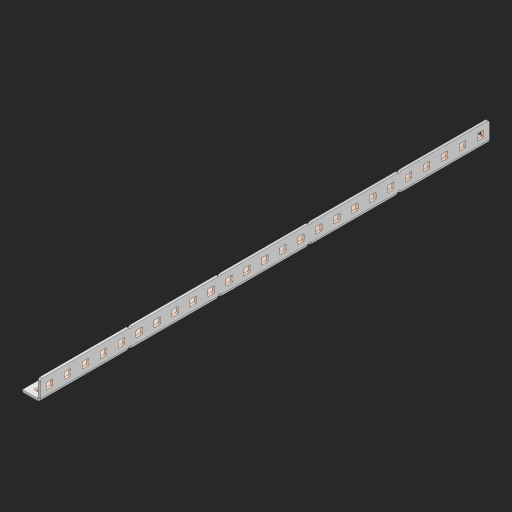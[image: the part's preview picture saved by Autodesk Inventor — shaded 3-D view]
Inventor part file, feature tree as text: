
AUTODESK INVENTOR PART (.ipt)
format: ipt  version: 2023 (Build 270158000, 158)  size: 854,528 bytes
history: native  units: in
note: dims shown in document units (in); Inventor stores cm internally (conversion verified against a paired STEP export)
features: other x55, extrude x49, sheet_metal_op x10, sketch x8, mirror x1, pattern_linear x1, chamfer x1
ambient origin geometry x8: Origin, YZ Plane, XZ Plane, XY Plane, X Axis, Y Axis, Z Axis, Center Point
bodies: Solid1 (feature_tree), Body (feature_tree)
feature tree (125):
  other  "Flange Pattern Plane"
  sheet_metal_op  "Flange Pattern"
  sheet_metal_op  "Body Pattern"
  other  "Arc Length"
  mirror  "Notch Mirror"
  pattern_linear  "Notch Pattern"  Spacing1=0.25in  [1 undecoded]
  chamfer  "End Chamfer"
  extrude  "Half Cut"  Depth=0.0625in
  sketch  "Sketch1"  dims[d0=1.5in]
  other  "Plate1"
  sketch  "Sketch2"  dims[d1=12.5in]
  other  "Plate2"
  sheet_metal_op  "Bend1"
  sheet_metal_op  "Corner1"
  sketch  "Sketch3"  dims[d2=0.0625in]
  other  "Flange Pattern Sketch"
  sketch  "Sketch7"  dims[d3=0.0625in]
  other  "Srf1"
  other  "Srf2"
  sketch  "Sketch8"  dims[d4=0.0312in]
  sketch  "Sketch9"  dims[d5=0.125in]
  other  "Srf91"
  sheet_metal_op  "Body Pattern Sketch"
  other  "Srf92"
  sketch  "Sketch13"  dims[d6=0.0625in]
  sketch  "Sketch14"  dims[d7=0.5in d8=90.0deg d9=0.0312in d10=0.25in d11=0.0625in d12=0.0625in d16=0.182in d17=0.02in d18=0.0625in d19=0.0in d20=0.25in d21=0.25in d46=0.172in d47=1.0in d48=0.0in d49=0.182in d50=0.02in d51=0.25in d52=0.25in d53=0.0625in d54=0.0in d55=0.172in d56=1.0in d57=0.0in d60=9.8425in d62=0.5in d63=0.3937in d65=0.5in d85=0.1473in d86=0.1782in d88=0.04in d89=0.0625in d90=0.0in d91=0.04in d92=0.0491in d95=2.5in d96=0.04in d97=0.25in d98=45.0deg d101=0.0in d102=2.497in d131=0.5in d132=9.8425in d134=0.5in d139=0.5in]
  other  "Srf856"
  other  "Srf1310"
  other  "Srf1311"
  other  "Srf1312"
  other  "Srf1376"
  other  "Srf1377"
  other  "Srf1728"
  other  "Srf1755"
  other  "Srf1878"
  other  "Srf1879"
  other  "Srf1880"
  other  "Srf1881"
  other  "Srf1882"
  other  "Srf1883"
  other  "Srf1884"
  other  "Srf1885"
  other  "Srf1886"
  other  "Srf1887"
  other  "Srf1888"
  other  "Srf1889"
  other  "Srf1890"
  other  "Srf1891"
  other  "Srf1892"
  other  "Srf1893"
  other  "Srf1894"
  other  "Srf1895"
  other  "Srf1896"
  other  "Srf1942"
  other  "Srf1943"
  other  "Srf1944"
  other  "Srf1945"
  other  "Srf1946"
  other  "Srf1947"
  other  "Srf1948"
  other  "Srf1949"
  other  "Srf1950"
  other  "Srf1951"
  other  "Srf1952"
  other  "Srf1953"
  other  "Srf1954"
  other  "Srf1955"
  other  "Srf1956"
  other  "Srf1957"
  other  "Srf1958"
  other  "Srf1959"
  other  "Srf1960"
  sheet_metal_op  "Flange Stamp"
  sheet_metal_op  "Flange Circle"
  sheet_metal_op  "Body Stamp"
  sheet_metal_op  "Body Circle"
  sheet_metal_op  "Notch"
  extrude  "ExtrusionSrf2"  Depth=0.0625in
  extrude  "ExtrusionSrf92"  Depth=0.5in
  extrude  "ExtrusionSrf856"  Depth=0.02in
  extrude  "ExtrusionSrf1310"  Depth=0.0625in
  extrude  "ExtrusionSrf1311"  TaperAngle=0.0deg  [1 undecoded]
  extrude  "ExtrusionSrf1312"  Depth=0.5in
  extrude  "ExtrusionSrf1376"  Depth=0.5in
  extrude  "ExtrusionSrf1377"  Depth=0.5in
  extrude  "ExtrusionSrf1728"  Depth=0.5in TaperAngle=0.0deg
  extrude  "ExtrusionSrf1755"  Depth=0.5in
  extrude  "ExtrusionSrf1878"  Depth=0.02in
  extrude  "ExtrusionSrf1879"  Depth=0.5in
  extrude  "ExtrusionSrf1880"  Depth=0.5in
  extrude  "ExtrusionSrf1881"  Depth=0.0625in
  extrude  "ExtrusionSrf1882"  TaperAngle=0.0deg  [1 undecoded]
  extrude  "ExtrusionSrf1883"  Depth=0.5in
  extrude  "ExtrusionSrf1884"  Depth=0.5in TaperAngle=0.0deg
  extrude  "ExtrusionSrf1885"  Depth=0.5in
  extrude  "ExtrusionSrf1886"  Depth=0.5in
  extrude  "ExtrusionSrf1887"  Depth=0.5in
  extrude  "ExtrusionSrf1888"  Depth=0.5in
  extrude  "ExtrusionSrf1889"  Depth=0.5in
  extrude  "ExtrusionSrf1890"  Depth=0.0625in
  extrude  "ExtrusionSrf1891"  TaperAngle=0.0deg  [1 undecoded]
  extrude  "ExtrusionSrf1892"  Depth=0.5in
  extrude  "ExtrusionSrf1893"  Depth=0.5in
  extrude  "ExtrusionSrf1894"  Depth=0.5in
  extrude  "ExtrusionSrf1895"  Depth=0.5in TaperAngle=45.0deg
  extrude  "ExtrusionSrf1896"  TaperAngle=0.0deg  [1 undecoded]
  extrude  "ExtrusionSrf1942"  Depth=0.5in
  extrude  "ExtrusionSrf1943"  Depth=0.5in
  extrude  "ExtrusionSrf1944"  Depth=0.5in
  extrude  "ExtrusionSrf1945"  Depth=0.5in
  extrude  "ExtrusionSrf1946"  Depth=0.5in
  extrude  "ExtrusionSrf1947"  [1 undecoded]
  extrude  "ExtrusionSrf1948"  [1 undecoded]
  extrude  "ExtrusionSrf1949"  [1 undecoded]
  extrude  "ExtrusionSrf1950"  [1 undecoded]
  extrude  "ExtrusionSrf1951"  [1 undecoded]
  extrude  "ExtrusionSrf1952"  [1 undecoded]
  extrude  "ExtrusionSrf1953"  [1 undecoded]
  extrude  "ExtrusionSrf1954"  [1 undecoded]
  extrude  "ExtrusionSrf1955"  [1 undecoded]
  extrude  "ExtrusionSrf1956"  [1 undecoded]
  extrude  "ExtrusionSrf1957"  [1 undecoded]
  extrude  "ExtrusionSrf1958"  [1 undecoded]
  extrude  "ExtrusionSrf1959"  [1 undecoded]
  extrude  "ExtrusionSrf1960"  [1 undecoded]
note: 19 required parameter values undecoded (feature->parameter linkage not recoverable at this tier; creation-order binding heuristic only, values carry confidence <= 0.55)
